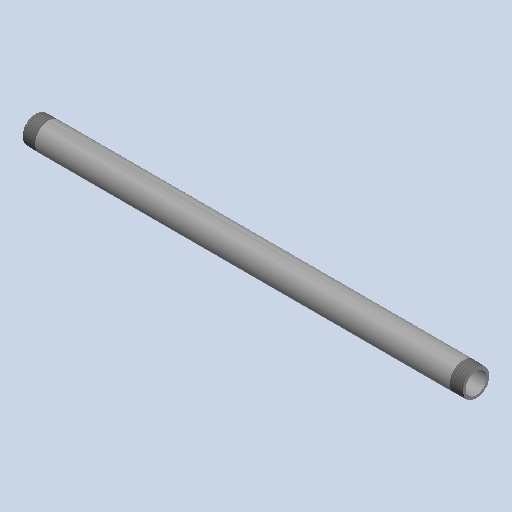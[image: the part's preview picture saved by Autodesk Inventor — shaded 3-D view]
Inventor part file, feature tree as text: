
AUTODESK INVENTOR PART (.ipt)
format: ipt  version: 2025 (Build 290162000, 162)  size: 158,208 bytes
history: native  units: mm (DEFAULTED — no unit token found)
features: other x8, revolve x1
ambient origin geometry x8: Origin, YZ Plane, XZ Plane, XY Plane, X Axis, Y Axis, Z Axis, Center Point
bodies: Solid1 (feature_tree)
feature tree (9):
  revolve  "Revolution1"  [1 undecoded]
  other  "Work Axis1"
  other  "Work Point5"
  other  "Work Axis2"
  other  "Work Point6"
  other  "Work Axis3"
  other  "Work Axis4"
  other  "Work Point7"
  other  "Work Point8"
note: 1 required parameter value undecoded (feature->parameter linkage not recoverable at this tier; creation-order binding heuristic only, values carry confidence <= 0.55)
